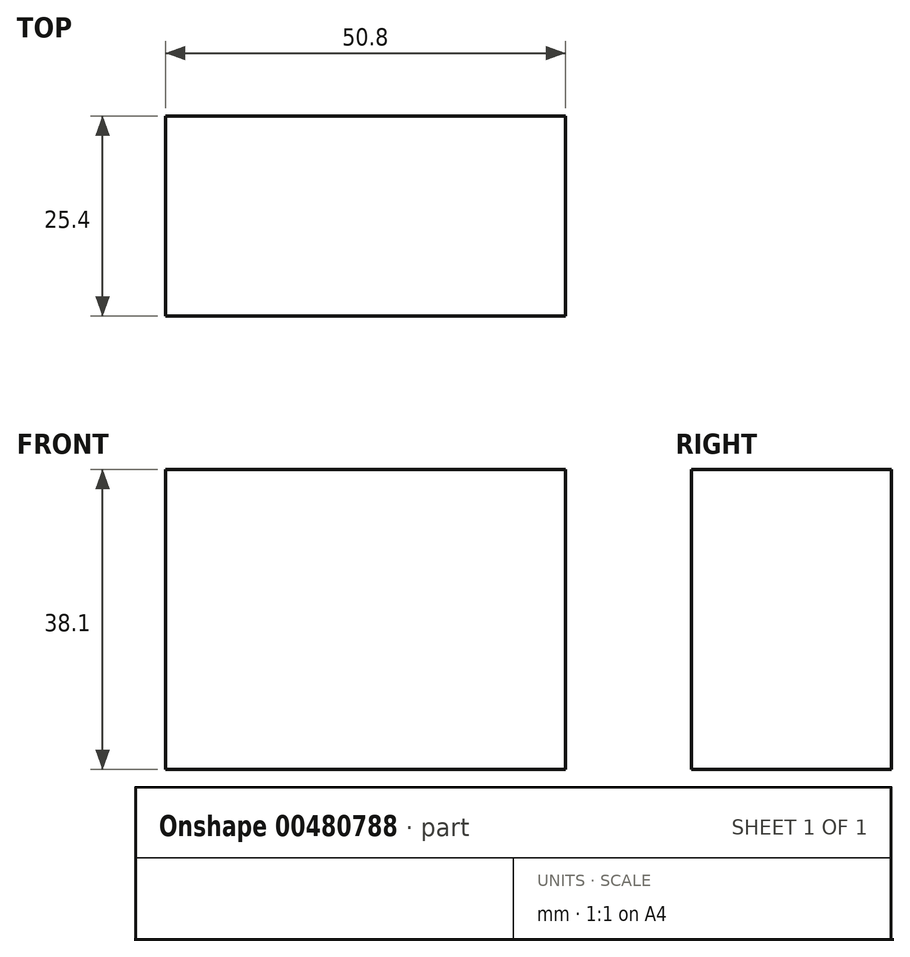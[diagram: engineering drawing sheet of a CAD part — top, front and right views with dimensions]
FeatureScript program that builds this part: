
annotation { "Feature Type Name" : "Feature", "Feature Type Description" : "" }
export const myFeature = defineFeature(function(context is Context, id is Id, definition is map)
    precondition{}
    {
        {
            var Q0;
            Q0=qCreatedBy(makeId("Front.planeOp"),FACE);
            var sketch = newSketch(context, id + "F0", { "sketchPlane" : qUnion([Q0])});
            skLineSegment(sketch, "E0.bottom", {"start": v(-30.16, -7.15) * mm, "end": v(20.64, -7.15) * mm});
            skLineSegment(sketch, "E0.top", {"start": v(-30.16, 30.95) * mm, "end": v(20.64, 30.95) * mm});
            skLineSegment(sketch, "E0.left", {"start": v(-30.16, -7.15) * mm, "end": v(-30.16, 30.95) * mm});
            skLineSegment(sketch, "E0.right", {"start": v(20.64, -7.15) * mm, "end": v(20.64, 30.95) * mm});
            skLineSegment(sketch, "E1", {"start": v(-30.16, 11.9) * mm, "end": v(20.64, 11.9) * mm});
            skSolve(sketch);
        }
        {
            var Q0;
            {var subQ0=sQuery(id+"F0.wireOp",EDGE,"E0.top");Q0=makeQuery(id+"F0.imprint","IMPRINT",FACE,{"disambiguationData":[TD([[makeQuery(id+"F0.imprint","IMPRINT",EDGE,{"derivedFrom":subQ0}),-1.0]])]});}
            var Q1;
            {var subQ0=sQuery(id+"F0.wireOp",EDGE,"E0.bottom");Q1=makeQuery(id+"F0.imprint","IMPRINT",FACE,{"disambiguationData":[TD([[makeQuery(id+"F0.imprint","IMPRINT",EDGE,{"derivedFrom":subQ0}),1.0]])]});}
            extrude(context, id + "F1", {"entities" : qUnion([Q0, Q1]), "depth" : 25.4 * mm});
        }
    });
